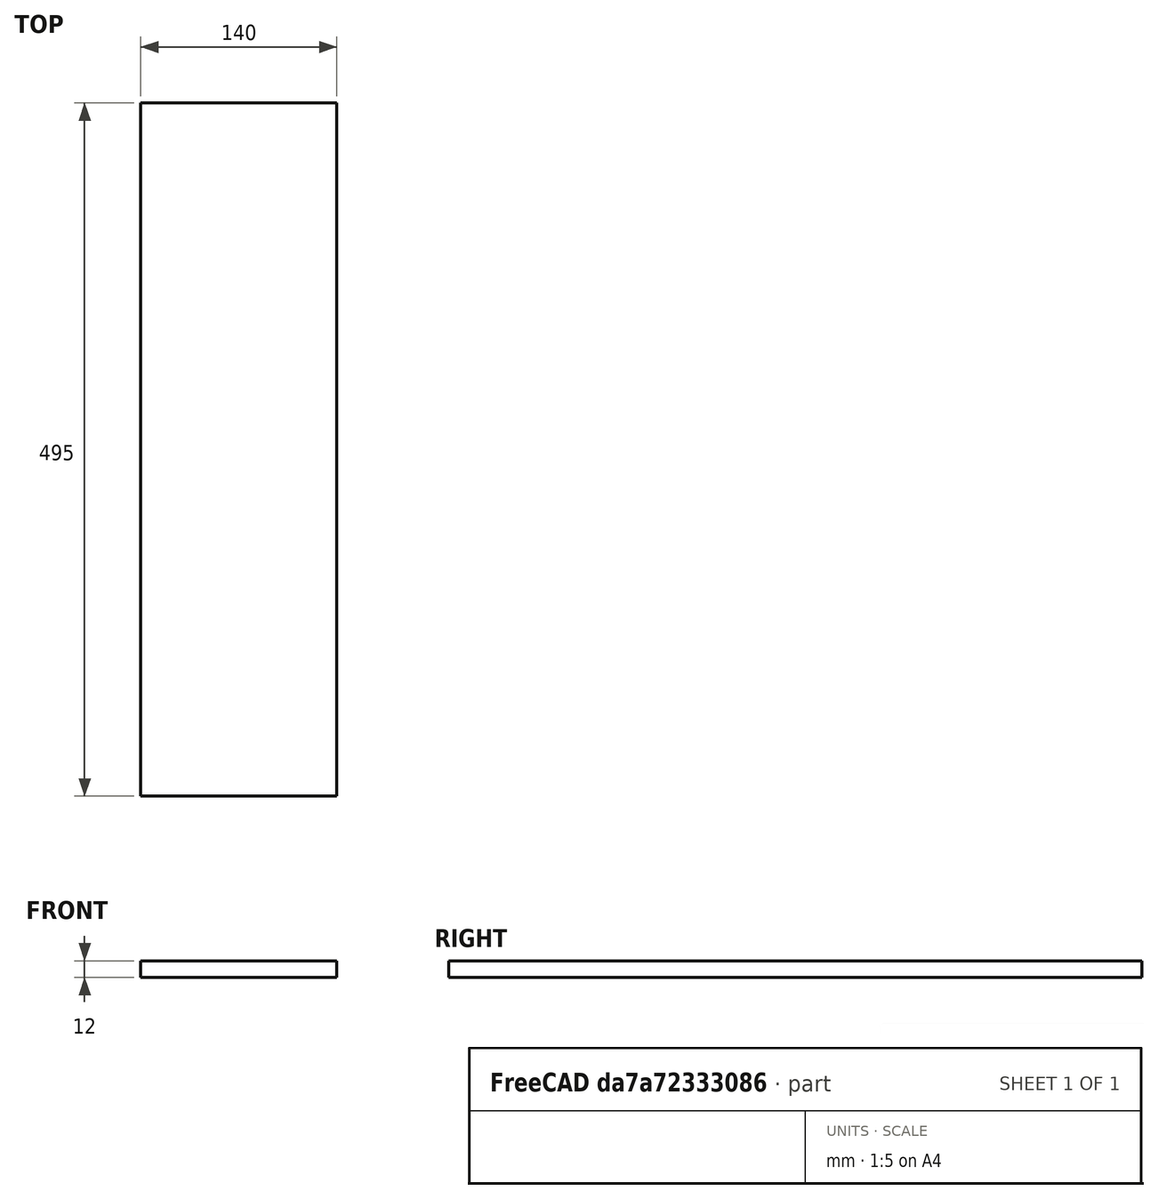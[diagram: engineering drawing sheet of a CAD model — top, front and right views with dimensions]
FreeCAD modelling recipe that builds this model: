
FCSTD DOCUMENT  (FreeCAD 0.20R29177 (Git))
Label: 1001_keyboard_floor_495_12
License: All rights reserved
LicenseURL: http://en.wikipedia.org/wiki/All_rights_reserved
objects: Sketcher::SketchObject×1, PartDesign::Pad×1, PartDesign::Body×1, Spreadsheet::Sheet×1
note: 4 computed .brp shape members not serialized (recipe doc carries the construction recipe); baked Part::Feature solids carry a one-line shape summary decoded from their .brp

FEATURE [Sketcher::SketchObject] Sketch
  FullyConstrained = true
  MapMode = 5
  Support = -> [XY_Plane]
  expr: Constraints[5] = <<xls>>.k_w
  expr: Constraints[6] = <<xls>>.k_d
  sketch-geometry (5):
    g0: LineSegment StartX=0 StartY=495 StartZ=0 EndX=140 EndY=495 EndZ=0
    g1: LineSegment StartX=140 StartY=495 StartZ=0 EndX=140 EndY=0 EndZ=0
    g2: LineSegment StartX=140 StartY=0 StartZ=0 EndX=0 EndY=0 EndZ=0
    g3: LineSegment StartX=0 StartY=0 StartZ=0 EndX=0 EndY=247.5 EndZ=0
    g4: LineSegment StartX=0 StartY=247.5 StartZ=0 EndX=0 EndY=495 EndZ=0
  constraints (14):
    c: Coincident(g0,g1)
    c: Coincident(g1,g2)
    c: Horizontal(g0)
    c: Horizontal(g2)
    c: Vertical(g1)
    c: DistanceY(g1,g1) = 495
    c: DistanceX(g0,g0) = 140
    c: Coincident(g3,g2)
    c: Coincident(g4,g0)
    c: Equal(g3,g4)
    c: Vertical(g4)
    c: Vertical(g3)
    c: Coincident(g3,g4)
    c: Coincident(g2,g-1)
FEATURE [PartDesign::Pad] Pad
  AllowMultiFace = false
  Direction = (0,0,1)
  Length = 12
  Length2 = 100
  Profile = -> Sketch
  ReferenceAxis = -> Sketch [N_Axis]
  Type = 0
  expr: Length = <<xls>>.k_t_0
FEATURE [PartDesign::Body] Body
  Group = -> [Sketch,Pad]
  Origin = -> Origin
  Tip = -> Pad
FEATURE [Spreadsheet::Sheet] Spreadsheet  label="xls"
  cells = B1=INHERITED; C1=Sperrholz Birke Phenol 2-seitig glatt 12 mm; B2=Thickness Front; D2=12; E2=mm; B3=Width Cabinet Floor; D3=495; E3=mm; B5=FLOOR; C5=Sperrholz Birke 12 mm; B6=Thickness; C6=k_t_0; D6(k_t_0)=12; E6=mm; B7=Width Nominal; D7==D3; F7=Floor width; G7=strutt; H7=strutt; I7=tolerance; B8=Width; C8=k_w; D8(k_w)=495; E8=mm; F8=495; G8=18; H8=18; I8=4; B9=Deapth Nominal; D9=150; B10=Deapth; C10=k_d; D10(k_d)=140; E10=mm
